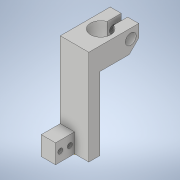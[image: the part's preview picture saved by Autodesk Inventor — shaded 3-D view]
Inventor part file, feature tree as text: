
AUTODESK INVENTOR PART (.ipt)
format: ipt  version: 2021 (Build 250183000, 183)  size: 191,488 bytes
history: native  units: mm
features: sketch x9, extrude x5, hole x4, other x2, plane x1, chamfer x1
ambient origin geometry x8: Origin, YZ Plane, XZ Plane, XY Plane, X Axis, Y Axis, Z Axis, Center Point
bodies: Solid1 (feature_tree)
feature tree (22):
  extrude  "Extrusion1"  Depth=30.0mm
  extrude  "Extrusion2"  Depth=7.0mm
  other  "Work Point1"
  plane  "Work Plane1"
  extrude  "Extrusion3"  Depth=4.5mm
  extrude  "Extrusion6"  Depth=6.0mm
  extrude  "Extrusion7"  Depth=6.0mm
  hole  "Hole2"  [1 undecoded]
  other  "Work Axis1"
  hole  "Hole3"  [1 undecoded]
  chamfer  "Chamfer1"  Distance=15.0mm
  hole  "Hole4"  [1 undecoded]
  hole  "Hole5"  [1 undecoded]
  sketch  "Sketch1"  dims[d0=3.5mm d1=30.0mm]
  sketch  "Sketch2"  dims[d2=9.0mm d3=0.0mm d4=7.0mm]
  sketch  "Sketch3"  dims[d5=12.25mm d6=0.0mm d7=4.5mm]
  sketch  "Sketch7"  dims[d8=4.5mm d9=6.0mm]
  sketch  "Sketch8"  dims[d10=6.0mm d11=0.0mm d14=3.75mm]
  sketch  "Sketch9"  dims[d42=6.4008mm d43=7.5mm]
  sketch  "Sketch10"  dims[d44=15.0mm d45=0.0mm d46=8.0mm]
  sketch  "Sketch13"  dims[d47=2.0mm]
  sketch  "Sketch14"  dims[d48=1.0mm d49=15.0mm d50=0.0mm d51=3.0mm d52=2.5mm d53=3.4mm d54=6.0mm d55=6.3mm d56=1.6mm d57=90.0deg d58=8.0mm d59=0.0mm d60=2.459mm d61=6.0mm d62=6.3mm d63=1.6mm d64=90.0deg d65=8.8mm d66=0.0mm d73=3.0mm d74=2.0mm d75=45.0deg d82=1.567mm d83=4.0mm d84=4.0mm d85=2.0mm d86=90.0deg d87=8.0mm d88=20.594885mm d91=3.0mm d92=4.5mm d93=1.567mm d94=4.0mm d95=4.0mm d96=2.0mm d97=90.0deg d98=8.0mm d99=20.594885mm d100=4.5mm d101=3.0mm d89=1.0mm d90=1.0mm]
note: 4 required parameter values undecoded (feature->parameter linkage not recoverable at this tier; creation-order binding heuristic only, values carry confidence <= 0.55)
